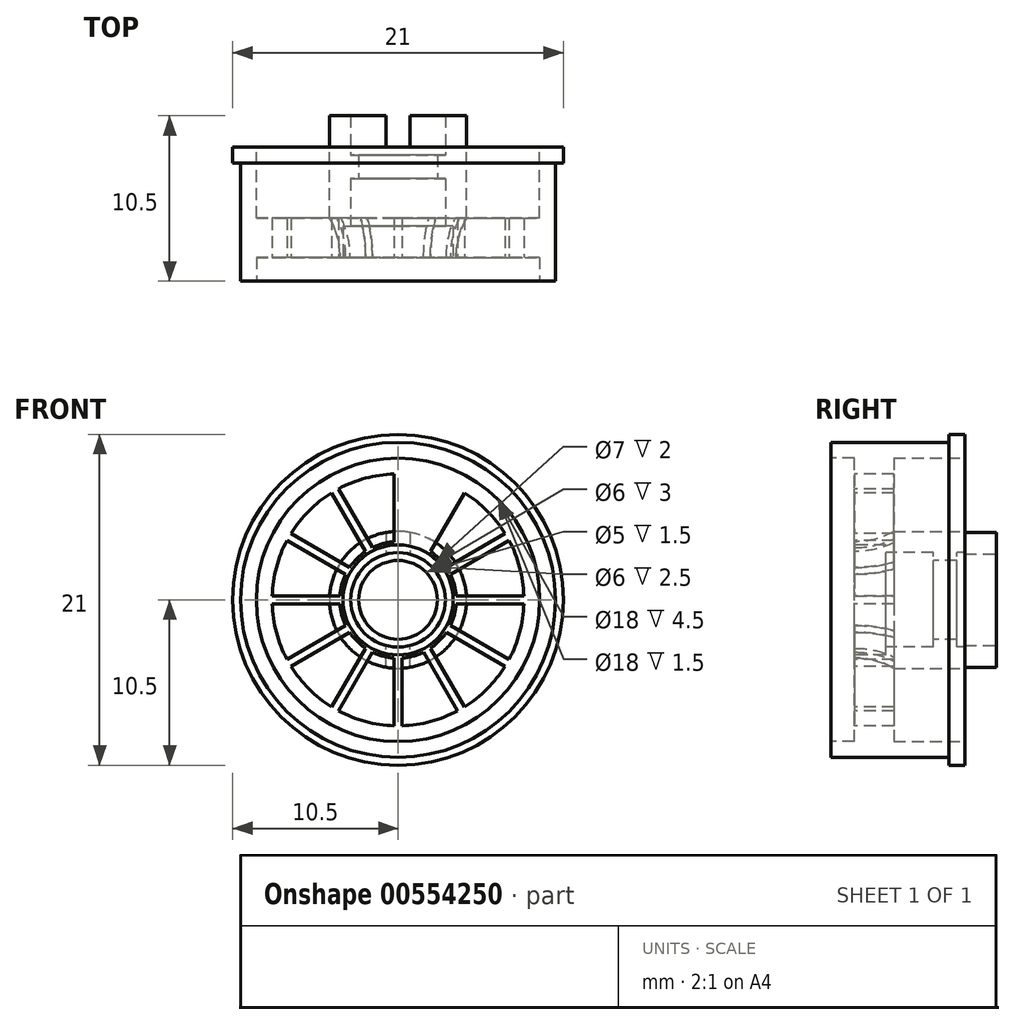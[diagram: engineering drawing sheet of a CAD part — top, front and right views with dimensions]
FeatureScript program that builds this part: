
annotation { "Feature Type Name" : "Feature", "Feature Type Description" : "" }
export const myFeature = defineFeature(function(context is Context, id is Id, definition is map)
    precondition{}
    {
        {
            var Q0;
            Q0=qCreatedBy(makeId("Front.planeOp"),FACE);
            var sketch = newSketch(context, id + "F0", { "sketchPlane" : qUnion([Q0])});
            skCircle(sketch, "E0", {"center": v(0, 0) * mm, "radius": 10.5 * mm});
            skSolve(sketch);
        }
        {
            var Q0;
            Q0=makeQuery(id+"F0.imprint","IMPRINT",FACE,{"disambiguationData":[TD([[makeQuery(id+"F0.imprint","IMPRINT",EDGE,{"derivedFrom":sQuery(id+"F0.wireOp",EDGE,"E0")}),1.0]])]});
            extrude(context, id + "F1", {"entities" : qUnion([Q0]), "depth" : 1 * mm});
        }
        {
            var Q0;
            Q0=makeQuery(id+"F1.opExtrude","CAP_FACE",FACE,{"disambiguationData":[OSD([sQuery(id+"F0.wireOp",EDGE,"E0")])],"isStart":false});
            var sketch = newSketch(context, id + "F2", { "sketchPlane" : qUnion([Q0])});
            skCircle(sketch, "E1", {"center": v(0, 0) * mm, "radius": 10 * mm});
            skSolve(sketch);
        }
        {
            var Q0;
            Q0=makeQuery(id+"F2.imprint","IMPRINT",FACE,{"disambiguationData":[TD([[makeQuery(id+"F2.imprint","IMPRINT",EDGE,{"derivedFrom":sQuery(id+"F2.wireOp",EDGE,"E1")}),1.0]])]});
            extrude(context, id + "F3", {"entities" : qUnion([Q0]), "operationType" : NewBodyOperationType.ADD, "depth" : 7.5 * mm});
        }
        {
            var Q0;
            Q0=makeQuery(id+"F3.opExtrude","CAP_FACE",FACE,{"disambiguationData":[OSD([sQuery(id+"F2.wireOp",EDGE,"E1")])],"isStart":false});
            var sketch = newSketch(context, id + "F4", { "sketchPlane" : qUnion([Q0])});
            skCircle(sketch, "E2", {"center": v(0, 0) * mm, "radius": 3.5 * mm});
            skSolve(sketch);
        }
        {
            var Q0;
            Q0=makeQuery(id+"F4.imprint","IMPRINT",FACE,{"disambiguationData":[TD([[makeQuery(id+"F4.imprint","IMPRINT",EDGE,{"derivedFrom":sQuery(id+"F4.wireOp",EDGE,"E2")}),1.0]])]});
            extrude(context, id + "F5", {"entities" : qUnion([Q0]), "operationType" : NewBodyOperationType.REMOVE, "oppositeDirection" : true, "depth" : 3.5 * mm});
        }
        {
            var Q0;
            Q0=makeQuery(id+"F5.boolean.opBoolean","COPY",FACE,{"derivedFrom":makeQuery(id+"F5.opExtrude","CAP_FACE",FACE,{"disambiguationData":[OSD([sQuery(id+"F4.wireOp",EDGE,"E2")])],"isStart":false})});
            var sketch = newSketch(context, id + "F6", { "sketchPlane" : qUnion([Q0])});
            skCircle(sketch, "E3", {"center": v(0, 0) * mm, "radius": 3 * mm});
            skSolve(sketch);
        }
        {
            var Q0;
            Q0=makeQuery(id+"F6.imprint","IMPRINT",FACE,{"disambiguationData":[TD([[makeQuery(id+"F6.imprint","IMPRINT",EDGE,{"derivedFrom":sQuery(id+"F6.wireOp",EDGE,"E3")}),1.0]])]});
            extrude(context, id + "F7", {"entities" : qUnion([Q0]), "operationType" : NewBodyOperationType.REMOVE, "oppositeDirection" : true, "depth" : 3 * mm});
        }
        {
            var Q0;
            Q0=makeQuery(id+"F7.boolean.opBoolean","COPY",FACE,{"derivedFrom":makeQuery(id+"F7.opExtrude","CAP_FACE",FACE,{"disambiguationData":[OSD([sQuery(id+"F6.wireOp",EDGE,"E3")])],"isStart":false})});
            var sketch = newSketch(context, id + "F8", { "sketchPlane" : qUnion([Q0])});
            skCircle(sketch, "E4", {"center": v(0, 0) * mm, "radius": 2.5 * mm});
            skSolve(sketch);
        }
        {
            var Q0;
            Q0=makeQuery(id+"F8.imprint","IMPRINT",FACE,{"disambiguationData":[TD([[makeQuery(id+"F8.imprint","IMPRINT",EDGE,{"derivedFrom":sQuery(id+"F8.wireOp",EDGE,"E4")}),1.0]])]});
            extrude(context, id + "F9", {"entities" : qUnion([Q0]), "operationType" : NewBodyOperationType.REMOVE, "oppositeDirection" : true, "depth" : 1.5 * mm});
        }
        {
            var Q0;
            Q0=makeQuery(id+"F9.boolean.opBoolean","COPY",FACE,{"derivedFrom":makeQuery(id+"F9.opExtrude","CAP_FACE",FACE,{"disambiguationData":[OSD([sQuery(id+"F8.wireOp",EDGE,"E4")])],"isStart":false})});
            var sketch = newSketch(context, id + "F10", { "sketchPlane" : qUnion([Q0])});
            skCircle(sketch, "E5", {"center": v(0, 0) * mm, "radius": 3 * mm});
            skSolve(sketch);
        }
        {
            var Q0;
            Q0=qSketchRegion(id+"F10",true);
            extrude(context, id + "F11", {"entities" : qUnion([Q0]), "operationType" : NewBodyOperationType.REMOVE, "oppositeDirection" : true, "depth" : 25 * mm});
        }
        {
            var Q0;
            Q0=makeQuery(id+"F3.opExtrude","CAP_FACE",FACE,{"disambiguationData":[OSD([sQuery(id+"F2.wireOp",EDGE,"E1")])],"isStart":false});
            var sketch = newSketch(context, id + "F12", { "sketchPlane" : qUnion([Q0])});
            skCircle(sketch, "E6", {"center": v(0, 0) * mm, "radius": 9 * mm});
            skSolve(sketch);
        }
        {
            var Q0;
            Q0=makeQuery(id+"F1.opExtrude","CAP_FACE",FACE,{"disambiguationData":[OSD([sQuery(id+"F0.wireOp",EDGE,"E0")])],"isStart":true});
            var sketch = newSketch(context, id + "F13", { "sketchPlane" : qUnion([Q0])});
            skCircle(sketch, "E7", {"center": v(0, 0) * mm, "radius": 9 * mm});
            skCircle(sketch, "E8", {"center": v(0, 0) * mm, "radius": 4.35 * mm});
            skSolve(sketch);
        }
        {
            var Q0;
            Q0=makeQuery(id+"F13.imprint","IMPRINT",FACE,{"disambiguationData":[TD([[makeQuery(id+"F13.imprint","IMPRINT",EDGE,{"derivedFrom":sQuery(id+"F13.wireOp",EDGE,"E7")}),1.0]])]});
            extrude(context, id + "F14", {"entities" : qUnion([Q0]), "operationType" : NewBodyOperationType.REMOVE, "oppositeDirection" : true, "depth" : 4.5 * mm});
        }
        {
            var Q0;
            Q0=makeQuery(id+"F12.imprint","IMPRINT",FACE,{"disambiguationData":[TD([[makeQuery(id+"F12.imprint","IMPRINT",EDGE,{"derivedFrom":sQuery(id+"F12.wireOp",EDGE,"E6")}),1.0]])]});
            extrude(context, id + "F15", {"entities" : qUnion([Q0]), "operationType" : NewBodyOperationType.REMOVE, "oppositeDirection" : true, "depth" : 1.5 * mm});
        }
        {
            var Q0;
            Q0=makeQuery(id+"F15.boolean.opBoolean","COPY",FACE,{"derivedFrom":makeQuery(id+"F15.opExtrude","CAP_FACE",FACE,{"disambiguationData":[OSD([sQuery(id+"F4.wireOp",EDGE,"E2"),sQuery(id+"F12.wireOp",EDGE,"E6")])],"isStart":false})});
            var sketch = newSketch(context, id + "F16", { "sketchPlane" : qUnion([Q0])});
            skCircle(sketch, "E9.0", {"center": v(0, 0) * mm, "radius": 8 * mm});
            skCircle(sketch, "E10.0", {"center": v(0, 0) * mm, "radius": 3.7 * mm});
            skLineSegment(sketch, "E11", {"start": v(-1.85, 3.2) * mm, "end": v(-4, 6.93) * mm});
            skLineSegment(sketch, "E12", {"start": v(0, 3.7) * mm, "end": v(0, 8) * mm});
            skLineSegment(sketch, "E13", {"start": v(-0.25, 3.7) * mm, "end": v(-0.25, 8) * mm});
            skLineSegment(sketch, "E14.0.MirrorCS", {"start": v(0.25, 3.7) * mm, "end": v(0.25, 8) * mm});
            skLineSegment(sketch, "E15", {"start": v(-2.06, 3.07) * mm, "end": v(-4.21, 6.8) * mm});
            skLineSegment(sketch, "E16.0.MirrorCS", {"start": v(-1.63, 3.32) * mm, "end": v(-3.78, 7.05) * mm});
            skLineSegment(sketch, "E17.1.0", {"start": v(-3.07, 2.06) * mm, "end": v(-6.8, 4.21) * mm});
            skLineSegment(sketch, "E17.2.0", {"start": v(-3.7, 0.25) * mm, "end": v(-8, 0.25) * mm});
            skLineSegment(sketch, "E17.2.1", {"start": v(-3.32, 1.63) * mm, "end": v(-7.05, 3.78) * mm});
            skLineSegment(sketch, "E17.3.0", {"start": v(-3.32, -1.63) * mm, "end": v(-7.05, -3.78) * mm});
            skLineSegment(sketch, "E17.3.1", {"start": v(-3.7, -0.25) * mm, "end": v(-8, -0.25) * mm});
            skLineSegment(sketch, "E17.4.0", {"start": v(-2.06, -3.07) * mm, "end": v(-4.21, -6.8) * mm});
            skLineSegment(sketch, "E17.4.1", {"start": v(-3.07, -2.06) * mm, "end": v(-6.8, -4.21) * mm});
            skLineSegment(sketch, "E17.5.0", {"start": v(-0.25, -3.7) * mm, "end": v(-0.25, -8) * mm});
            skLineSegment(sketch, "E17.5.1", {"start": v(-1.63, -3.32) * mm, "end": v(-3.78, -7.05) * mm});
            skLineSegment(sketch, "E17.6.0", {"start": v(1.63, -3.32) * mm, "end": v(3.78, -7.05) * mm});
            skLineSegment(sketch, "E17.6.1", {"start": v(0.25, -3.7) * mm, "end": v(0.25, -8) * mm});
            skLineSegment(sketch, "E17.7.0", {"start": v(3.07, -2.06) * mm, "end": v(6.8, -4.21) * mm});
            skLineSegment(sketch, "E17.7.1", {"start": v(2.06, -3.07) * mm, "end": v(4.21, -6.8) * mm});
            skLineSegment(sketch, "E17.8.0", {"start": v(3.7, -0.25) * mm, "end": v(8, -0.25) * mm});
            skLineSegment(sketch, "E17.8.1", {"start": v(3.32, -1.63) * mm, "end": v(7.05, -3.78) * mm});
            skLineSegment(sketch, "E17.9.0", {"start": v(3.32, 1.63) * mm, "end": v(7.05, 3.78) * mm});
            skLineSegment(sketch, "E17.9.1", {"start": v(3.7, 0.25) * mm, "end": v(8, 0.25) * mm});
            skLineSegment(sketch, "E17.10.0", {"start": v(2.06, 3.07) * mm, "end": v(4.21, 6.8) * mm});
            skLineSegment(sketch, "E17.10.1", {"start": v(3.07, 2.06) * mm, "end": v(6.8, 4.21) * mm});
            skLineSegment(sketch, "E17.11.1", {"start": v(1.63, 3.32) * mm, "end": v(3.78, 7.05) * mm});
            skSolve(sketch);
        }
        {
            var Q0;
            {var subQ1=sQuery(id+"F16.wireOp",EDGE,"E13");Q0=makeQuery(id+"F16.imprint","IMPRINT",FACE,{"disambiguationData":[TD([[makeQuery(id+"F16.imprint","IMPRINT",EDGE,{"derivedFrom":subQ1}),1.0]])]});}
            var Q1;
            {var subQ1=sQuery(id+"F16.wireOp",EDGE,"E14.0.MirrorCS");Q1=makeQuery(id+"F16.imprint","IMPRINT",FACE,{"disambiguationData":[TD([[makeQuery(id+"F16.imprint","IMPRINT",EDGE,{"derivedFrom":subQ1}),-1.0]])]});}
            var Q2;
            {var subQ1=sQuery(id+"F16.wireOp",EDGE,"E17.10.0");Q2=makeQuery(id+"F16.imprint","IMPRINT",FACE,{"disambiguationData":[TD([[makeQuery(id+"F16.imprint","IMPRINT",EDGE,{"derivedFrom":subQ1}),-1.0]])]});}
            var Q3;
            {var subQ1=sQuery(id+"F16.wireOp",EDGE,"E17.9.0");Q3=makeQuery(id+"F16.imprint","IMPRINT",FACE,{"disambiguationData":[TD([[makeQuery(id+"F16.imprint","IMPRINT",EDGE,{"derivedFrom":subQ1}),-1.0]])]});}
            var Q4;
            {var subQ1=sQuery(id+"F16.wireOp",EDGE,"E17.8.0");Q4=makeQuery(id+"F16.imprint","IMPRINT",FACE,{"disambiguationData":[TD([[makeQuery(id+"F16.imprint","IMPRINT",EDGE,{"derivedFrom":subQ1}),-1.0]])]});}
            var Q5;
            {var subQ1=sQuery(id+"F16.wireOp",EDGE,"E17.7.0");Q5=makeQuery(id+"F16.imprint","IMPRINT",FACE,{"disambiguationData":[TD([[makeQuery(id+"F16.imprint","IMPRINT",EDGE,{"derivedFrom":subQ1}),-1.0]])]});}
            var Q6;
            {var subQ2=sQuery(id+"F16.wireOp",EDGE,"E17.1.0");Q6=makeQuery(id+"F16.imprint","IMPRINT",FACE,{"disambiguationData":[TD([[makeQuery(id+"F16.imprint","IMPRINT",EDGE,{"derivedFrom":subQ2}),-1.0]])]});}
            var Q7;
            {var subQ2=sQuery(id+"F16.wireOp",EDGE,"E17.2.0");Q7=makeQuery(id+"F16.imprint","IMPRINT",FACE,{"disambiguationData":[TD([[makeQuery(id+"F16.imprint","IMPRINT",EDGE,{"derivedFrom":subQ2}),-1.0]])]});}
            var Q8;
            {var subQ2=sQuery(id+"F16.wireOp",EDGE,"E17.3.0");Q8=makeQuery(id+"F16.imprint","IMPRINT",FACE,{"disambiguationData":[TD([[makeQuery(id+"F16.imprint","IMPRINT",EDGE,{"derivedFrom":subQ2}),-1.0]])]});}
            var Q9;
            {var subQ1=sQuery(id+"F16.wireOp",EDGE,"E17.4.0");Q9=makeQuery(id+"F16.imprint","IMPRINT",FACE,{"disambiguationData":[TD([[makeQuery(id+"F16.imprint","IMPRINT",EDGE,{"derivedFrom":subQ1}),-1.0]])]});}
            var Q10;
            {var subQ1=sQuery(id+"F16.wireOp",EDGE,"E17.5.0");Q10=makeQuery(id+"F16.imprint","IMPRINT",FACE,{"disambiguationData":[TD([[makeQuery(id+"F16.imprint","IMPRINT",EDGE,{"derivedFrom":subQ1}),-1.0]])]});}
            var Q11;
            {var subQ1=sQuery(id+"F16.wireOp",EDGE,"E17.6.0");Q11=makeQuery(id+"F16.imprint","IMPRINT",FACE,{"disambiguationData":[TD([[makeQuery(id+"F16.imprint","IMPRINT",EDGE,{"derivedFrom":subQ1}),-1.0]])]});}
            extrude(context, id + "F17", {"entities" : qUnion([Q0, Q1, Q2, Q3, Q4, Q5, Q6, Q7, Q8, Q9, Q10, Q11]), "operationType" : NewBodyOperationType.REMOVE, "oppositeDirection" : true, "depth" : 2.5 * mm});
        }
        {
            var Q0;
            {var subQ0=sQuery(id+"F16.wireOp",EDGE,"E10.0");Q0=makeQuery(id+"F17.boolean.opBoolean","COPY",EDGE,{"derivedFrom":makeQuery(id+"F17.opExtrude","CAP_EDGE",EDGE,{"disambiguationData":[OSD([subQ0]),TDD([makeQuery(id+"F16.imprint","IMPRINT",EDGE,{"disambiguationData":[TD([[makeQuery(id+"F16.imprint","INTERSECT",VERTEX,{"derivedFrom":[subQ0,sQuery(id+"F16.wireOp",EDGE,"E17.1.0")]}),1.0]])],"derivedFrom":subQ0})])],"isStart":false})});}
            var Q1;
            {var subQ0=sQuery(id+"F16.wireOp",EDGE,"E10.0");Q1=makeQuery(id+"F17.boolean.opBoolean","COPY",EDGE,{"derivedFrom":makeQuery(id+"F17.opExtrude","CAP_EDGE",EDGE,{"disambiguationData":[OSD([subQ0]),TDD([makeQuery(id+"F16.imprint","IMPRINT",EDGE,{"disambiguationData":[TD([[makeQuery(id+"F16.imprint","INTERSECT",VERTEX,{"derivedFrom":[subQ0,sQuery(id+"F16.wireOp",EDGE,"E13")]}),-1.0]])],"derivedFrom":subQ0})])],"isStart":false})});}
            var Q2;
            {var subQ0=sQuery(id+"F16.wireOp",EDGE,"E10.0");Q2=makeQuery(id+"F17.boolean.opBoolean","COPY",EDGE,{"derivedFrom":makeQuery(id+"F17.opExtrude","CAP_EDGE",EDGE,{"disambiguationData":[OSD([subQ0]),TDD([makeQuery(id+"F16.imprint","IMPRINT",EDGE,{"disambiguationData":[TD([[makeQuery(id+"F16.imprint","INTERSECT",VERTEX,{"derivedFrom":[subQ0,sQuery(id+"F16.wireOp",EDGE,"E14.0.MirrorCS")]}),1.0]])],"derivedFrom":subQ0})])],"isStart":false})});}
            var Q3;
            {var subQ0=sQuery(id+"F16.wireOp",EDGE,"E10.0");Q3=makeQuery(id+"F17.boolean.opBoolean","COPY",EDGE,{"derivedFrom":makeQuery(id+"F17.opExtrude","CAP_EDGE",EDGE,{"disambiguationData":[OSD([subQ0]),TDD([makeQuery(id+"F16.imprint","IMPRINT",EDGE,{"disambiguationData":[TD([[makeQuery(id+"F16.imprint","INTERSECT",VERTEX,{"derivedFrom":[subQ0,sQuery(id+"F16.wireOp",EDGE,"E17.10.0")]}),1.0]])],"derivedFrom":subQ0})])],"isStart":false})});}
            var Q4;
            {var subQ0=sQuery(id+"F16.wireOp",EDGE,"E10.0");Q4=makeQuery(id+"F17.boolean.opBoolean","COPY",EDGE,{"derivedFrom":makeQuery(id+"F17.opExtrude","CAP_EDGE",EDGE,{"disambiguationData":[OSD([subQ0]),TDD([makeQuery(id+"F16.imprint","IMPRINT",EDGE,{"disambiguationData":[TD([[makeQuery(id+"F16.imprint","INTERSECT",VERTEX,{"derivedFrom":[subQ0,sQuery(id+"F16.wireOp",EDGE,"E17.2.0")]}),1.0]])],"derivedFrom":subQ0})])],"isStart":false})});}
            var Q5;
            {var subQ0=sQuery(id+"F16.wireOp",EDGE,"E10.0");Q5=makeQuery(id+"F17.boolean.opBoolean","COPY",EDGE,{"derivedFrom":makeQuery(id+"F17.opExtrude","CAP_EDGE",EDGE,{"disambiguationData":[OSD([subQ0]),TDD([makeQuery(id+"F16.imprint","IMPRINT",EDGE,{"disambiguationData":[TD([[makeQuery(id+"F16.imprint","INTERSECT",VERTEX,{"derivedFrom":[subQ0,sQuery(id+"F16.wireOp",EDGE,"E17.3.0")]}),1.0]])],"derivedFrom":subQ0})])],"isStart":false})});}
            var Q6;
            {var subQ0=sQuery(id+"F16.wireOp",EDGE,"E10.0");Q6=makeQuery(id+"F17.boolean.opBoolean","COPY",EDGE,{"derivedFrom":makeQuery(id+"F17.opExtrude","CAP_EDGE",EDGE,{"disambiguationData":[OSD([subQ0]),TDD([makeQuery(id+"F16.imprint","IMPRINT",EDGE,{"disambiguationData":[TD([[makeQuery(id+"F16.imprint","INTERSECT",VERTEX,{"derivedFrom":[subQ0,sQuery(id+"F16.wireOp",EDGE,"E17.9.0")]}),1.0]])],"derivedFrom":subQ0})])],"isStart":false})});}
            var Q7;
            {var subQ0=sQuery(id+"F16.wireOp",EDGE,"E10.0");Q7=makeQuery(id+"F17.boolean.opBoolean","COPY",EDGE,{"derivedFrom":makeQuery(id+"F17.opExtrude","CAP_EDGE",EDGE,{"disambiguationData":[OSD([subQ0]),TDD([makeQuery(id+"F16.imprint","IMPRINT",EDGE,{"disambiguationData":[TD([[makeQuery(id+"F16.imprint","INTERSECT",VERTEX,{"derivedFrom":[subQ0,sQuery(id+"F16.wireOp",EDGE,"E17.8.0")]}),1.0]])],"derivedFrom":subQ0})])],"isStart":false})});}
            var Q8;
            {var subQ0=sQuery(id+"F16.wireOp",EDGE,"E10.0");Q8=makeQuery(id+"F17.boolean.opBoolean","COPY",EDGE,{"derivedFrom":makeQuery(id+"F17.opExtrude","CAP_EDGE",EDGE,{"disambiguationData":[OSD([subQ0]),TDD([makeQuery(id+"F16.imprint","IMPRINT",EDGE,{"disambiguationData":[TD([[makeQuery(id+"F16.imprint","INTERSECT",VERTEX,{"derivedFrom":[subQ0,sQuery(id+"F16.wireOp",EDGE,"E17.7.0")]}),1.0]])],"derivedFrom":subQ0})])],"isStart":false})});}
            var Q9;
            {var subQ0=sQuery(id+"F16.wireOp",EDGE,"E10.0");Q9=makeQuery(id+"F17.boolean.opBoolean","COPY",EDGE,{"derivedFrom":makeQuery(id+"F17.opExtrude","CAP_EDGE",EDGE,{"disambiguationData":[OSD([subQ0]),TDD([makeQuery(id+"F16.imprint","IMPRINT",EDGE,{"disambiguationData":[TD([[makeQuery(id+"F16.imprint","INTERSECT",VERTEX,{"derivedFrom":[subQ0,sQuery(id+"F16.wireOp",EDGE,"E17.6.0")]}),1.0]])],"derivedFrom":subQ0})])],"isStart":false})});}
            var Q10;
            {var subQ0=sQuery(id+"F16.wireOp",EDGE,"E10.0");Q10=makeQuery(id+"F17.boolean.opBoolean","COPY",EDGE,{"derivedFrom":makeQuery(id+"F17.opExtrude","CAP_EDGE",EDGE,{"disambiguationData":[OSD([subQ0]),TDD([makeQuery(id+"F16.imprint","IMPRINT",EDGE,{"disambiguationData":[TD([[makeQuery(id+"F16.imprint","INTERSECT",VERTEX,{"derivedFrom":[subQ0,sQuery(id+"F16.wireOp",EDGE,"E17.5.0")]}),1.0]])],"derivedFrom":subQ0})])],"isStart":false})});}
            var Q11;
            {var subQ0=sQuery(id+"F16.wireOp",EDGE,"E10.0");Q11=makeQuery(id+"F17.boolean.opBoolean","COPY",EDGE,{"derivedFrom":makeQuery(id+"F17.opExtrude","CAP_EDGE",EDGE,{"disambiguationData":[OSD([subQ0]),TDD([makeQuery(id+"F16.imprint","IMPRINT",EDGE,{"disambiguationData":[TD([[makeQuery(id+"F16.imprint","INTERSECT",VERTEX,{"derivedFrom":[subQ0,sQuery(id+"F16.wireOp",EDGE,"E17.4.0")]}),1.0]])],"derivedFrom":subQ0})])],"isStart":false})});}
            fillet(context, id + "F18", {"entities" : qUnion([Q0, Q1, Q2, Q3, Q4, Q5, Q6, Q7, Q8, Q9, Q10, Q11]), "radius" : 5 * mm, "tangentPropagation" : true, "allowEdgeOverflow" : false});
        }
        {
            var Q0;
            Q0=makeQuery(id+"F14.boolean.opBoolean","SPLIT",FACE,{"disambiguationData":[TD([makeQuery(id+"F11.boolean.opBoolean","COPY",FACE,{"derivedFrom":makeQuery(id+"F11.opExtrude","SWEPT_FACE",FACE,{"disambiguationData":[OSD([sQuery(id+"F10.wireOp",EDGE,"E5")])]})})])],"derivedFrom":makeQuery(id+"F1.opExtrude","CAP_FACE",FACE,{"disambiguationData":[OSD([sQuery(id+"F0.wireOp",EDGE,"E0")])],"isStart":true})});
            extrude(context, id + "F19", {"entities" : qUnion([Q0]), "operationType" : NewBodyOperationType.ADD, "depth" : 2 * mm});
        }
        {
            var Q0;
            Q0=makeQuery(id+"F19.opExtrude","CAP_FACE",FACE,{"disambiguationData":[OSD([sQuery(id+"F0.wireOp",EDGE,"E0")])],"isStart":false});
            var sketch = newSketch(context, id + "F20", { "sketchPlane" : qUnion([Q0])});
            skLineSegment(sketch, "E18", {"start": v(0, 3) * mm, "end": v(0, 4.35) * mm});
            skLineSegment(sketch, "E19", {"start": v(-0.75, 4.28) * mm, "end": v(-0.75, 2.9) * mm});
            skLineSegment(sketch, "E20.0.MirrorCS", {"start": v(0.75, 4.28) * mm, "end": v(0.75, 2.9) * mm});
            skLineSegment(sketch, "E21", {"start": v(0, 0) * mm, "end": v(2.07, 0) * mm});
            skLineSegment(sketch, "E22.0.MirrorCS", {"start": v(-0.75, -4.28) * mm, "end": v(-0.75, -2.9) * mm});
            skLineSegment(sketch, "E23.0.MirrorCS", {"start": v(0.75, -4.28) * mm, "end": v(0.75, -2.9) * mm});
            skSolve(sketch);
        }
        {
            var Q0;
            {var subQ2=sQuery(id+"F20.wireOp",EDGE,"E18");Q0=makeQuery(id+"F20.imprint","IMPRINT",FACE,{"disambiguationData":[TD([[makeQuery(id+"F20.imprint","IMPRINT",EDGE,{"derivedFrom":subQ2}),1.0]])]});}
            var Q1;
            {var subQ2=sQuery(id+"F20.wireOp",EDGE,"E18");Q1=makeQuery(id+"F20.imprint","IMPRINT",FACE,{"disambiguationData":[TD([[makeQuery(id+"F20.imprint","IMPRINT",EDGE,{"derivedFrom":subQ2}),-1.0]])]});}
            var Q2;
            {var subQ2=sQuery(id+"F20.wireOp",EDGE,"E22.0.MirrorCS");Q2=makeQuery(id+"F20.imprint","IMPRINT",FACE,{"disambiguationData":[TD([[makeQuery(id+"F20.imprint","IMPRINT",EDGE,{"derivedFrom":subQ2}),-1.0]])]});}
            extrude(context, id + "F21", {"entities" : qUnion([Q0, Q1, Q2]), "operationType" : NewBodyOperationType.REMOVE, "oppositeDirection" : true, "depth" : 2 * mm});
        }
    });
